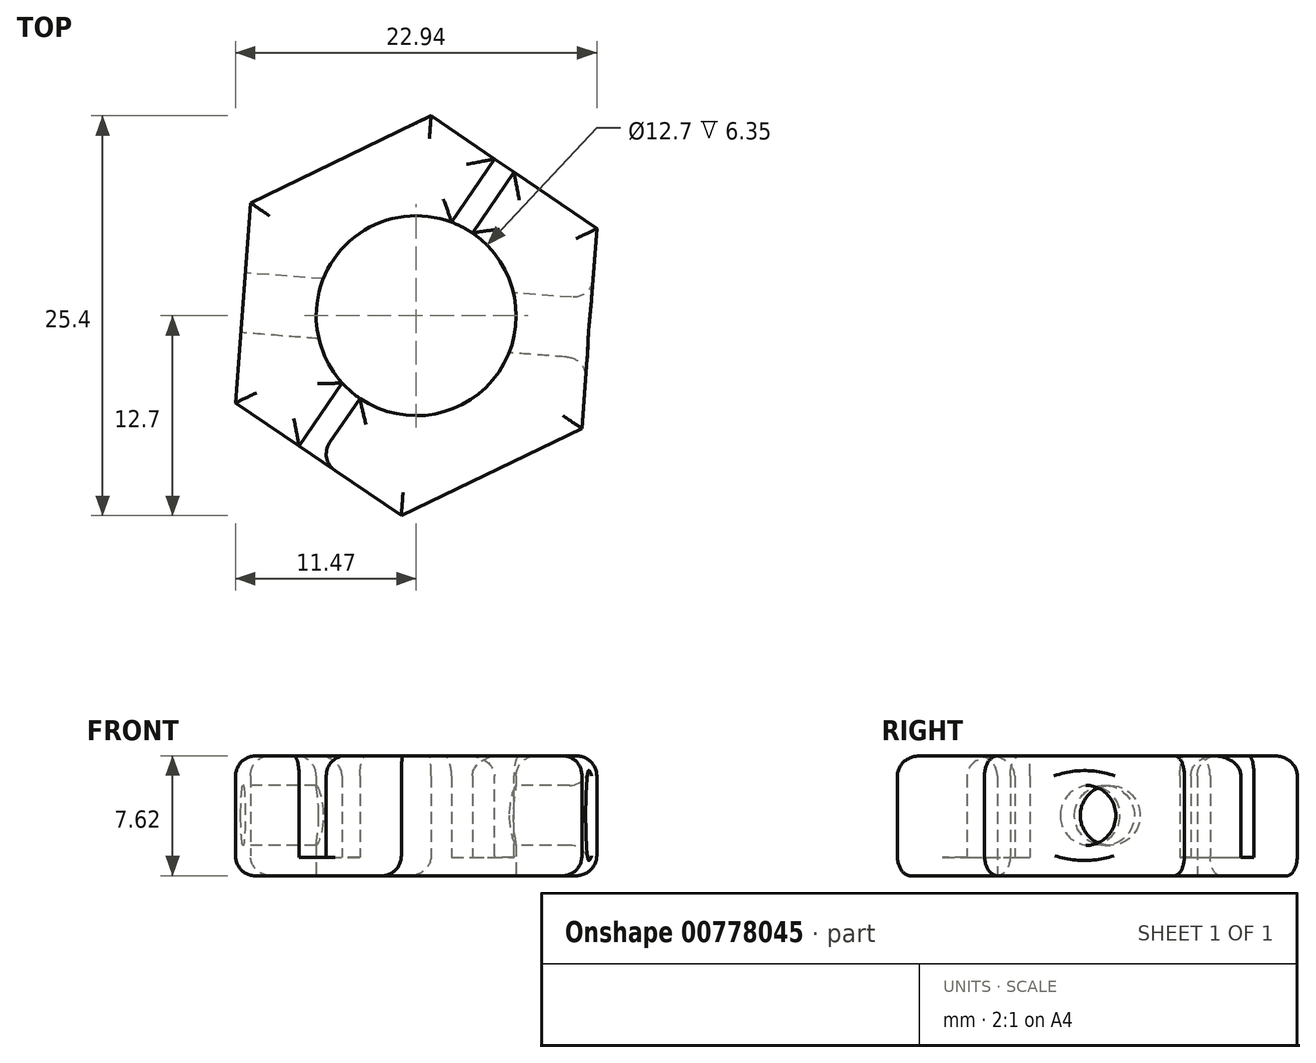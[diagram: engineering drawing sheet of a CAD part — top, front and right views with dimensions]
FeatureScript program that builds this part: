
annotation { "Feature Type Name" : "Feature", "Feature Type Description" : "" }
export const myFeature = defineFeature(function(context is Context, id is Id, definition is map)
    precondition{}
    {
        {
            var Q0;
            Q0=qCreatedBy(makeId("Top.planeOp"),FACE);
            var sketch = newSketch(context, id + "F0", { "sketchPlane" : qUnion([Q0])});
            skCircle(sketch, "E0.cCircle", {"center": v(0, 0) * mm, "radius": 11.03 * mm, "construction": true});
            skLineSegment(sketch, "E0.0", {"start": v(0.94, 12.7) * mm, "end": v(11.47, 5.53) * mm});
            skLineSegment(sketch, "E0.1", {"start": v(11.47, 5.53) * mm, "end": v(10.53, -7.17) * mm});
            skLineSegment(sketch, "E0.2", {"start": v(10.53, -7.17) * mm, "end": v(-0.94, -12.7) * mm});
            skLineSegment(sketch, "E0.3", {"start": v(-0.94, -12.7) * mm, "end": v(-11.47, -5.53) * mm});
            skLineSegment(sketch, "E0.4", {"start": v(-11.47, -5.53) * mm, "end": v(-10.53, 7.17) * mm});
            skLineSegment(sketch, "E0.5", {"start": v(-10.53, 7.17) * mm, "end": v(0.94, 12.7) * mm});
            skPoint(sketch, "E0.0.midPoint", {"position": v(6.2, 9.12) * mm});
            skSolve(sketch);
        }
        {
            var Q0;
            Q0=makeQuery(id+"F0.imprint","IMPRINT",FACE,{"disambiguationData":[TD([[makeQuery(id+"F0.imprint","IMPRINT",EDGE,{"derivedFrom":sQuery(id+"F0.wireOp",EDGE,"E0.0")}),-1.0]])]});
            extrude(context, id + "F1", {"entities" : qUnion([Q0]), "depth" : 7.62 * mm, "offsetDistance" : 25.4 * mm});
        }
        {
            var Q0;
            Q0=makeQuery(id+"F1.opExtrude","CAP_FACE",FACE,{"disambiguationData":[OSD([sQuery(id+"F0.wireOp",EDGE,"E0.0"),sQuery(id+"F0.wireOp",EDGE,"E0.1"),sQuery(id+"F0.wireOp",EDGE,"E0.2"),sQuery(id+"F0.wireOp",EDGE,"E0.3"),sQuery(id+"F0.wireOp",EDGE,"E0.4"),sQuery(id+"F0.wireOp",EDGE,"E0.5")])],"isStart":true});
            var sketch = newSketch(context, id + "F2", { "sketchPlane" : qUnion([Q0])});
            skCircle(sketch, "E1", {"center": v(0, 0) * mm, "radius": 6.35 * mm});
            skSolve(sketch);
        }
        {
            var Q0;
            Q0 = qSketchRegion(id + "F2", true);
            extrude(context, id + "F3", {"entities" : qUnion([Q0]), "operationType" : NewBodyOperationType.REMOVE, "oppositeDirection" : true, "depth" : 25.4 * mm, "offsetDistance" : 25.4 * mm});
        }
        {
            var Q0;
            Q0=makeQuery(id+"F1.opExtrude","SWEPT_FACE",FACE,{"disambiguationData":[OSD([sQuery(id+"F0.wireOp",EDGE,"E0.4")])]});
            var sketch = newSketch(context, id + "F4", { "sketchPlane" : qUnion([Q0])});
            skCircle(sketch, "E2", {"center": v(0, 3.83) * mm, "radius": 1.9 * mm});
            skSolve(sketch);
        }
        {
            var Q0;
            Q0=makeQuery(id+"F4.imprint","IMPRINT",FACE,{"disambiguationData":[TD([[makeQuery(id+"F4.imprint","IMPRINT",EDGE,{"derivedFrom":sQuery(id+"F4.wireOp",EDGE,"E2")}),1.0]])]});
            extrude(context, id + "F5", {"entities" : qUnion([Q0]), "operationType" : NewBodyOperationType.REMOVE, "oppositeDirection" : true, "depth" : 34.24 * mm, "offsetDistance" : 25.4 * mm});
        }
        {
            var Q0;
            Q0=makeQuery(id+"F1.opExtrude","SWEPT_FACE",FACE,{"disambiguationData":[OSD([sQuery(id+"F0.wireOp",EDGE,"E0.0")])]});
            var sketch = newSketch(context, id + "F6", { "sketchPlane" : qUnion([Q0])});
            skPoint(sketch, "E3.firstSnap0", {"position": v(0, 7.62) * mm});
            skLineSegment(sketch, "E3.bottom", {"start": v(0, 1.15) * mm, "end": v(1.49, 1.15) * mm});
            skLineSegment(sketch, "E3.top", {"start": v(0, 29.1) * mm, "end": v(1.49, 29.1) * mm});
            skLineSegment(sketch, "E3.left", {"start": v(0, 1.15) * mm, "end": v(0, 29.1) * mm});
            skLineSegment(sketch, "E3.right", {"start": v(1.49, 1.15) * mm, "end": v(1.49, 29.1) * mm});
            skSolve(sketch);
        }
        {
            var Q0;
            {var subQ0=sQuery(id+"F6.wireOp",EDGE,"E3.top");Q0=makeQuery(id+"F6.imprint","IMPRINT",FACE,{"disambiguationData":[TD([[makeQuery(id+"F6.imprint","IMPRINT",EDGE,{"derivedFrom":subQ0}),-1.0]])]});}
            var Q1;
            {var subQ0=sQuery(id+"F6.wireOp",EDGE,"E3.bottom");Q1=makeQuery(id+"F6.imprint","IMPRINT",FACE,{"disambiguationData":[TD([[makeQuery(id+"F6.imprint","IMPRINT",EDGE,{"derivedFrom":subQ0}),1.0]])]});}
            extrude(context, id + "F7", {"entities" : qUnion([Q0, Q1]), "operationType" : NewBodyOperationType.REMOVE, "oppositeDirection" : true, "depth" : 32.5 * mm, "offsetDistance" : 25.4 * mm});
        }
        {
            var Q0;
            Q0=makeQuery(id+"F7.boolean.opBoolean","INTERSECT",EDGE,{"disambiguationData":[OD(1.0)],"derivedFrom":[makeQuery(id+"F1.opExtrude","CAP_FACE",FACE,{"disambiguationData":[OSD([sQuery(id+"F0.wireOp",EDGE,"E0.0"),sQuery(id+"F0.wireOp",EDGE,"E0.1"),sQuery(id+"F0.wireOp",EDGE,"E0.2"),sQuery(id+"F0.wireOp",EDGE,"E0.3"),sQuery(id+"F0.wireOp",EDGE,"E0.4"),sQuery(id+"F0.wireOp",EDGE,"E0.5")])],"isStart":false}),makeQuery(id+"F7.opExtrude","SWEPT_FACE",FACE,{"disambiguationData":[OSD([sQuery(id+"F6.wireOp",EDGE,"E3.left")])]})]});
            var Q1;
            Q1=makeQuery(id+"F7.boolean.opBoolean","INTERSECT",EDGE,{"derivedFrom":[makeQuery(id+"F1.opExtrude","SWEPT_FACE",FACE,{"disambiguationData":[OSD([sQuery(id+"F0.wireOp",EDGE,"E0.3")])]}),makeQuery(id+"F7.opExtrude","SWEPT_FACE",FACE,{"disambiguationData":[OSD([sQuery(id+"F6.wireOp",EDGE,"E3.left")])]})]});
            var Q2;
            {var subQ0=sQuery(id+"F0.wireOp",EDGE,"E0.5");var subQ1=sQuery(id+"F0.wireOp",EDGE,"E0.4");var subQ2=sQuery(id+"F0.wireOp",EDGE,"E0.3");var subQ3=sQuery(id+"F0.wireOp",EDGE,"E0.0");Q2=makeQuery(id+"F7.boolean.opBoolean","SPLIT",FACE,{"disambiguationData":[TD([makeQuery(id+"F1.opExtrude","SWEPT_FACE",FACE,{"disambiguationData":[OSD([subQ1])]})])],"derivedFrom":makeQuery(id+"F1.opExtrude","CAP_FACE",FACE,{"disambiguationData":[OSD([subQ3,sQuery(id+"F0.wireOp",EDGE,"E0.1"),sQuery(id+"F0.wireOp",EDGE,"E0.2"),subQ2,subQ1,subQ0])],"isStart":false})});}
            var Q3;
            {var subQ0=sQuery(id+"F0.wireOp",EDGE,"E0.2");var subQ1=sQuery(id+"F0.wireOp",EDGE,"E0.1");var subQ2=sQuery(id+"F0.wireOp",EDGE,"E0.3");var subQ3=sQuery(id+"F0.wireOp",EDGE,"E0.0");Q3=makeQuery(id+"F7.boolean.opBoolean","SPLIT",FACE,{"disambiguationData":[TD([makeQuery(id+"F1.opExtrude","SWEPT_FACE",FACE,{"disambiguationData":[OSD([subQ1])]})])],"derivedFrom":makeQuery(id+"F1.opExtrude","CAP_FACE",FACE,{"disambiguationData":[OSD([subQ3,subQ1,subQ0,subQ2,sQuery(id+"F0.wireOp",EDGE,"E0.4"),sQuery(id+"F0.wireOp",EDGE,"E0.5")])],"isStart":false})});}
            var Q4;
            Q4=makeQuery(id+"F5.boolean.opBoolean","INTERSECT",EDGE,{"derivedFrom":[makeQuery(id+"F1.opExtrude","SWEPT_FACE",FACE,{"disambiguationData":[OSD([sQuery(id+"F0.wireOp",EDGE,"E0.1")])]}),makeQuery(id+"F5.opExtrude","SWEPT_FACE",FACE,{"disambiguationData":[OSD([sQuery(id+"F4.wireOp",EDGE,"E2")])]})]});
            var Q5;
            Q5=makeQuery(id+"F5.boolean.opBoolean","COPY",EDGE,{"derivedFrom":makeQuery(id+"F5.opExtrude","CAP_EDGE",EDGE,{"disambiguationData":[OSD([sQuery(id+"F4.wireOp",EDGE,"E2")])],"isStart":true})});
            var Q6;
            Q6=makeQuery(id+"F3.boolean.opBoolean","COPY",EDGE,{"derivedFrom":makeQuery(id+"F3.opExtrude","CAP_EDGE",EDGE,{"disambiguationData":[OSD([sQuery(id+"F2.wireOp",EDGE,"E1")])],"isStart":true})});
            var Q7;
            Q7=makeQuery(id+"F1.opExtrude","CAP_EDGE",EDGE,{"disambiguationData":[OSD([sQuery(id+"F0.wireOp",EDGE,"E0.1")])],"isStart":false});
            var Q8;
            Q8=makeQuery(id+"F1.opExtrude","CAP_EDGE",EDGE,{"disambiguationData":[OSD([sQuery(id+"F0.wireOp",EDGE,"E0.0")])],"isStart":true});
            var Q9;
            Q9=makeQuery(id+"F1.opExtrude","CAP_EDGE",EDGE,{"disambiguationData":[OSD([sQuery(id+"F0.wireOp",EDGE,"E0.1")])],"isStart":true});
            var Q10;
            Q10=makeQuery(id+"F1.opExtrude","CAP_EDGE",EDGE,{"disambiguationData":[OSD([sQuery(id+"F0.wireOp",EDGE,"E0.4")])],"isStart":true});
            var Q11;
            Q11=makeQuery(id+"F1.opExtrude","CAP_EDGE",EDGE,{"disambiguationData":[OSD([sQuery(id+"F0.wireOp",EDGE,"E0.2")])],"isStart":true});
            fillet(context, id + "F8", {"entities" : qUnion([Q0, Q1, Q2, Q3, Q4, Q5, Q6, Q7, Q8, Q9, Q10, Q11]), "radius" : 1.27 * mm, "tangentPropagation" : true, "allowEdgeOverflow" : false});
        }
    });
